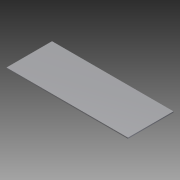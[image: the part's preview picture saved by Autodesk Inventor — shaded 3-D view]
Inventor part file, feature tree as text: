
AUTODESK INVENTOR PART (.ipt)
format: ipt  version: 2012 (Build 160160000, 160)  size: 73,728 bytes
history: native  units: in
note: dims shown in document units (in); Inventor stores cm internally (conversion verified against a paired STEP export)
features: extrude x1, sketch x1
ambient origin geometry x8: Origin, YZ Plane, XZ Plane, XY Plane, X Axis, Y Axis, Z Axis, Center Point
bodies: Solid1 (feature_tree)
feature tree (2):
  extrude  "Extrusion1"  Depth=0.2in
  sketch  "Sketch1"  dims[d0=24.0in d1=0.2in d2=9.0in d3=0.0in]
